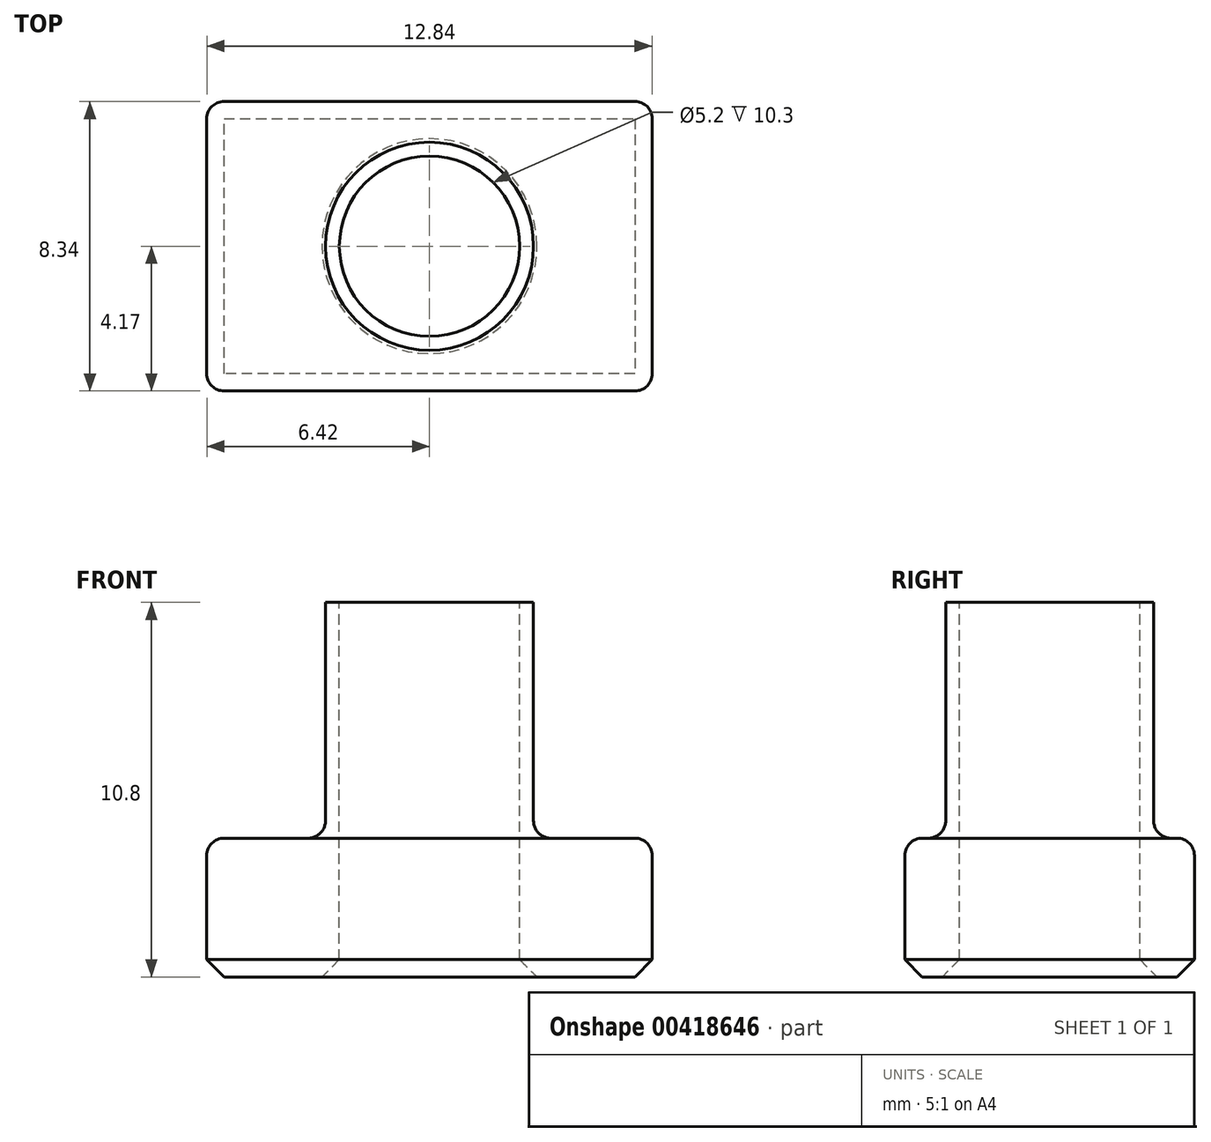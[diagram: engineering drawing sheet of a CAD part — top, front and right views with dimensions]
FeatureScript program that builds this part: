
annotation { "Feature Type Name" : "Feature", "Feature Type Description" : "" }
export const myFeature = defineFeature(function(context is Context, id is Id, definition is map)
    precondition{}
    {
        {
            var Q0;
            Q0=qCreatedBy(makeId("Top.planeOp"),FACE);
            var sketch = newSketch(context, id + "F0", { "sketchPlane" : qUnion([Q0])});
            skLineSegment(sketch, "E0.bottom", {"start": v(6.42, -4.18) * mm, "end": v(-6.42, -4.18) * mm});
            skLineSegment(sketch, "E0.top", {"start": v(6.42, 4.17) * mm, "end": v(-6.42, 4.17) * mm});
            skLineSegment(sketch, "E0.left", {"start": v(6.42, -4.18) * mm, "end": v(6.42, 4.17) * mm});
            skLineSegment(sketch, "E0.right", {"start": v(-6.42, -4.18) * mm, "end": v(-6.42, 4.17) * mm});
            skPoint(sketch, "E0.middle", {"position": v(0, 0) * mm});
            skSolve(sketch);
        }
        {
            var Q0;
            Q0 = qSketchRegion(id + "F0", true);
            extrude(context, id + "F1", {"entities" : qUnion([Q0]), "depth" : 4 * mm});
        }
        {
            var Q0;
            Q0=makeQuery(id+"F1.opExtrude","CAP_FACE",FACE,{"disambiguationData":[OSD([sQuery(id+"F0.wireOp",EDGE,"E0.bottom"),sQuery(id+"F0.wireOp",EDGE,"E0.top"),sQuery(id+"F0.wireOp",EDGE,"E0.left"),sQuery(id+"F0.wireOp",EDGE,"E0.right")])],"isStart":false});
            var sketch = newSketch(context, id + "F2", { "sketchPlane" : qUnion([Q0])});
            skCircle(sketch, "E1", {"center": v(0, 0) * mm, "radius": 3 * mm});
            skSolve(sketch);
        }
        {
            var Q0;
            Q0 = qSketchRegion(id + "F2", true);
            extrude(context, id + "F3", {"entities" : qUnion([Q0]), "operationType" : NewBodyOperationType.ADD, "depth" : 6.8 * mm});
        }
        {
            var Q0;
            Q0=makeQuery(id+"F3.opExtrude","CAP_FACE",FACE,{"disambiguationData":[OSD([sQuery(id+"F2.wireOp",EDGE,"E1")])],"isStart":false});
            var sketch = newSketch(context, id + "F4", { "sketchPlane" : qUnion([Q0])});
            skCircle(sketch, "E2", {"center": v(0, 0) * mm, "radius": 2.6 * mm});
            skSolve(sketch);
        }
        {
            var Q0;
            Q0 = qSketchRegion(id + "F4", true);
            extrude(context, id + "F5", {"entities" : qUnion([Q0]), "operationType" : NewBodyOperationType.REMOVE, "endBound" : BoundingType.THROUGH_ALL, "oppositeDirection" : true, "depth" : 25 * mm});
        }
        {
            var Q0;
            Q0=makeQuery(id+"F1.opExtrude","SWEPT_EDGE",EDGE,{"disambiguationData":[OSD([sQuery(id+"F0.wireOp",EDGE,"E0.top"),sQuery(id+"F0.wireOp",EDGE,"E0.right")])]});
            var Q1;
            Q1=makeQuery(id+"F1.opExtrude","SWEPT_EDGE",EDGE,{"disambiguationData":[OSD([sQuery(id+"F0.wireOp",EDGE,"E0.top"),sQuery(id+"F0.wireOp",EDGE,"E0.left")])]});
            var Q2;
            Q2=makeQuery(id+"F1.opExtrude","SWEPT_EDGE",EDGE,{"disambiguationData":[OSD([sQuery(id+"F0.wireOp",EDGE,"E0.bottom"),sQuery(id+"F0.wireOp",EDGE,"E0.left")])]});
            var Q3;
            Q3=makeQuery(id+"F1.opExtrude","SWEPT_EDGE",EDGE,{"disambiguationData":[OSD([sQuery(id+"F0.wireOp",EDGE,"E0.bottom"),sQuery(id+"F0.wireOp",EDGE,"E0.right")])]});
            fillet(context, id + "F6", {"entities" : qUnion([Q0, Q1, Q2, Q3]), "radius" : .5 * mm, "tangentPropagation" : true, "allowEdgeOverflow" : false});
        }
        {
            var Q0;
            Q0=makeQuery(id+"F1.opExtrude","CAP_FACE",FACE,{"disambiguationData":[OSD([sQuery(id+"F0.wireOp",EDGE,"E0.bottom"),sQuery(id+"F0.wireOp",EDGE,"E0.top"),sQuery(id+"F0.wireOp",EDGE,"E0.left"),sQuery(id+"F0.wireOp",EDGE,"E0.right")])],"isStart":false});
            fillet(context, id + "F7", {"entities" : qUnion([Q0]), "radius" : 0.5 * mm, "tangentPropagation" : true, "allowEdgeOverflow" : false});
        }
        {
            var Q0;
            Q0=makeQuery(id+"F1.opExtrude","CAP_FACE",FACE,{"disambiguationData":[OSD([sQuery(id+"F0.wireOp",EDGE,"E0.bottom"),sQuery(id+"F0.wireOp",EDGE,"E0.top"),sQuery(id+"F0.wireOp",EDGE,"E0.left"),sQuery(id+"F0.wireOp",EDGE,"E0.right")])],"isStart":true});
            chamfer(context, id + "F8", {"entities" : qUnion([Q0]), "width" : 0.5 * mm, "tangentPropagation" : true});
        }
    });
